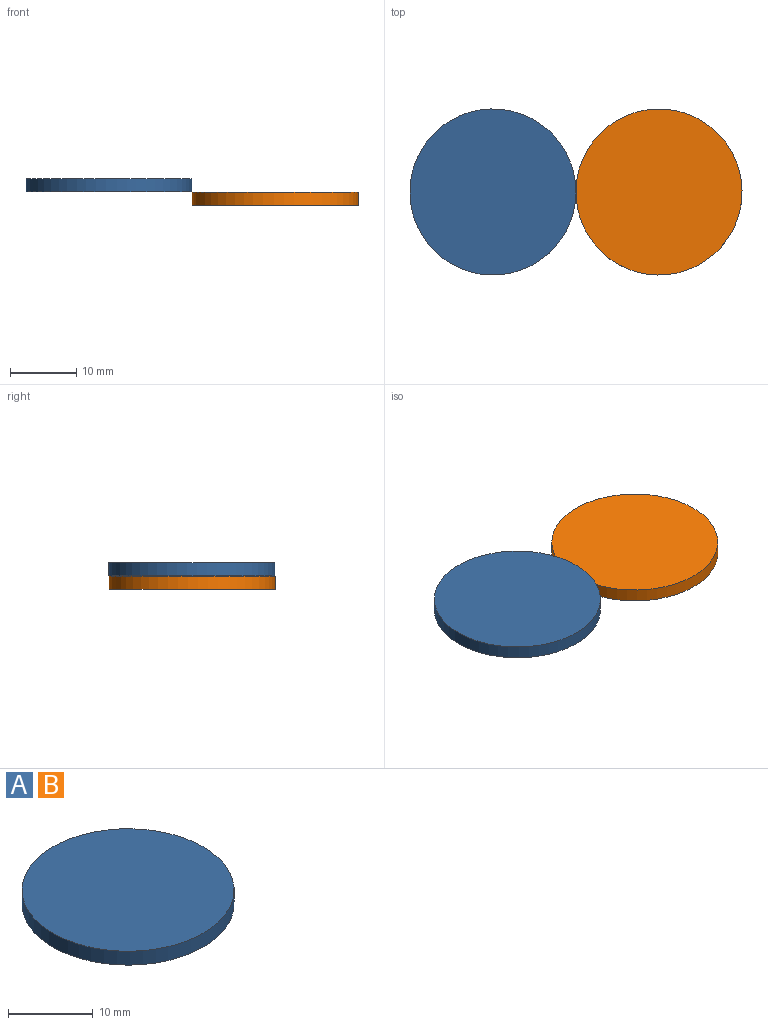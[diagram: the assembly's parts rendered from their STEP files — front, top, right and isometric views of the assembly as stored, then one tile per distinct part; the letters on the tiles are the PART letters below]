
ASSEMBLY  parts=2 mates=1
PART A: 3 faces, bbox 25x25x2 mm
  f0: cylinder r=12.5mm len=25mm, axis (0,0,-1), area 157.1mm2, adj f1,f2
  f1: plane 25x25mm, normal (0,0,1), area 490.9mm2, adj f0
  f2: plane 25x25mm, normal (0,0,-1), area 490.9mm2, adj f0
PART B: same geometry as A
PLACE A t=(-9.6,18.09,15.53)mm fixed
PLACE B rot(axis=(0,0,-1),41.5deg) t=(15.4,18.09,13.53)mm
MATE pin_slot B.f0 <-> A.f0  axis (0,0,1) through (15.4,18.09,15.53)mm
